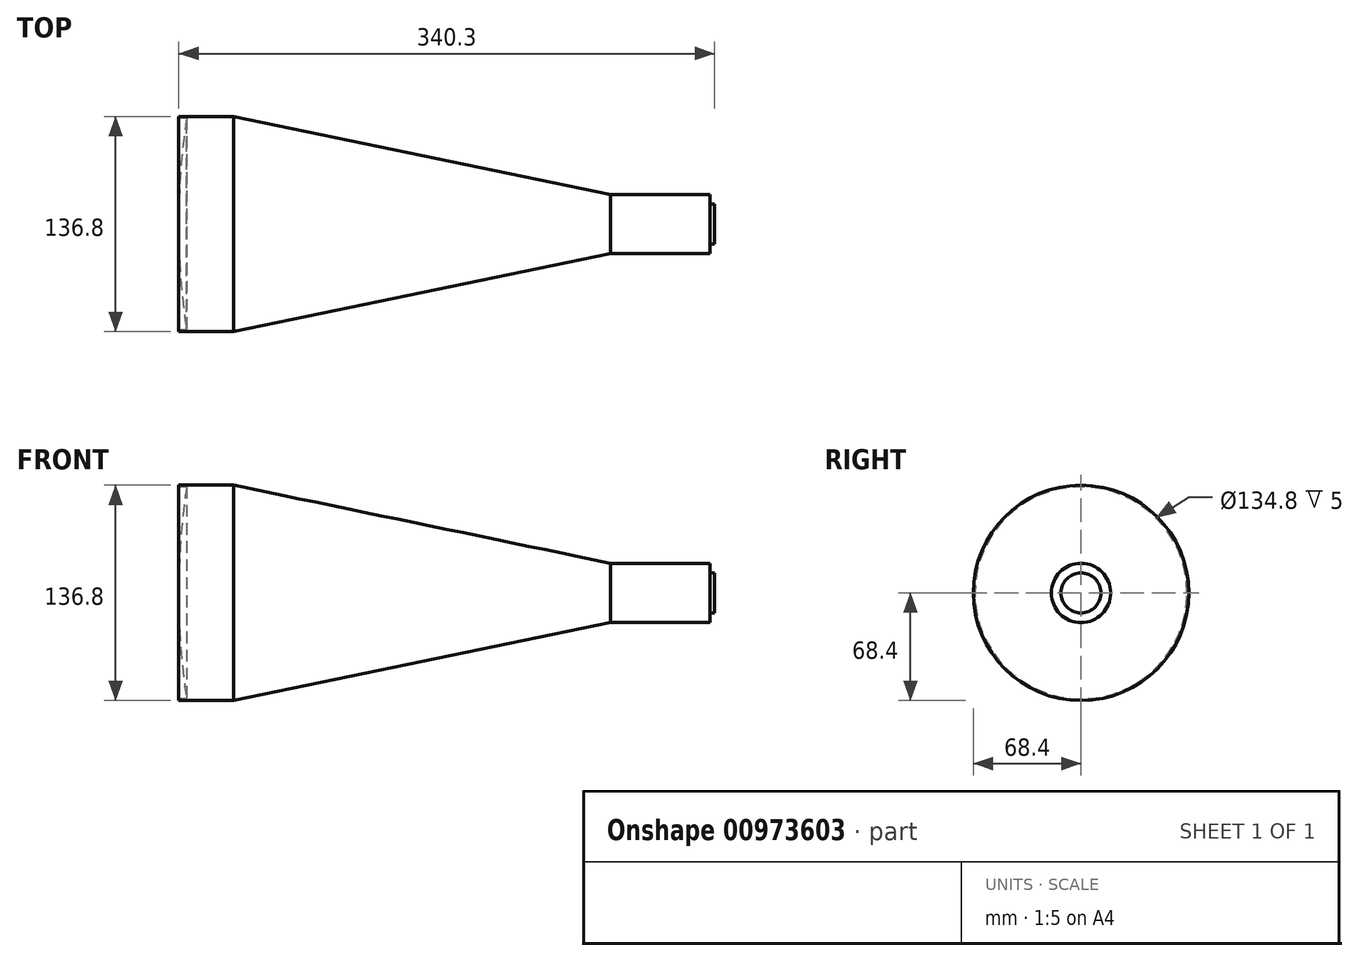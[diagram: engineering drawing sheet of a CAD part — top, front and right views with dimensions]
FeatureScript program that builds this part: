
annotation { "Feature Type Name" : "Feature", "Feature Type Description" : "" }
export const myFeature = defineFeature(function(context is Context, id is Id, definition is map)
    precondition{}
    {
        {
            var Q0;
            Q0=qCreatedBy(makeId("Front.planeOp"),FACE);
            var sketch = newSketch(context, id + "F0", { "sketchPlane" : qUnion([Q0])});
            skLineSegment(sketch, "E0", {"start": v(0, 0) * mm, "end": v(0, 12.7) * mm});
            skLineSegment(sketch, "E1", {"start": v(0, 12.7) * mm, "end": v(-3, 12.7) * mm});
            skLineSegment(sketch, "E2", {"start": v(-3, 12.7) * mm, "end": v(-3, 18.85) * mm});
            skLineSegment(sketch, "E3", {"start": v(-3, 18.85) * mm, "end": v(-66.1, 18.85) * mm});
            skLineSegment(sketch, "E4", {"start": v(-305.3, 68.4) * mm, "end": v(-340.3, 68.4) * mm});
            skLineSegment(sketch, "E5", {"start": v(-340.3, 0) * mm, "end": v(0, 0) * mm});
            skLineSegment(sketch, "E6", {"start": v(-305.3, 68.4) * mm, "end": v(-66.1, 18.85) * mm});
            skLineSegment(sketch, "E7", {"start": v(-340.3, 68.4) * mm, "end": v(-340.3, 67.4) * mm});
            skLineSegment(sketch, "E8", {"start": v(-340.3, 67.4) * mm, "end": v(-335.3, 67.4) * mm});
            skArc(sketch, "E9", {"start": v(-335.3, 67.4) * mm, "mid": v(-339.05, 33.8) * mm, "end": v(-340.3, 0) * mm});
            skSolve(sketch);
        }
        {
            var Q0;
            Q0=qSketchRegion(id+"F0",true);
            var Q1;
            Q1=sQuery(id+"F0.wireOp",EDGE,"E5");
            revolve(context, id + "F1", {"surfaceOperationType" : NewSurfaceOperationType.NEW, "entities" : qUnion([Q0]), "axis" : qUnion([Q1]), "revolveType" : RevolveType.FULL});
        }
    });
